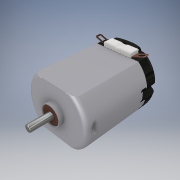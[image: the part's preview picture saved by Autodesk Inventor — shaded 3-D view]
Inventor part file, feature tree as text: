
AUTODESK INVENTOR PART (.ipt)
format: ipt  version: 2019 (Build 230136000, 136)  size: 1,063,424 bytes
history: native  units: mm
features: extrude x26, sketch x20, fillet x18, projected_geometry x6, plane x4, chamfer x3, mirror x2
ambient origin geometry x8: Origin, YZ Plane, XZ Plane, XY Plane, X Axis, Y Axis, Z Axis, Center Point
bodies: Solid1 (feature_tree)
feature tree (79):
  sketch  "Sketch1"  dims[d0=20.0mm d1=15.0mm d2=25.0mm d3=0.0mm d4=1.5mm]
  extrude  "Extrusion1"  Depth=15.0mm
  fillet  "Fillet1"  Radius=25.0mm
  fillet  "Fillet2"  Radius=1.5mm
  plane  "Work Plane1"
  extrude  "Extrusion2"  Depth=25.0mm TaperAngle=0.0deg
  extrude  "Extrusion3"  Depth=0.01mm TaperAngle=0.0deg
  extrude  "Extrusion4"  Depth=10.0mm
  sketch  "Sketch5"  dims[d12=10.0mm d13=4.0mm]
  extrude  "Extrusion5"  Depth=2.5mm
  extrude  "Extrusion6"  Depth=5.5mm
  extrude  "Extrusion7"  Depth=2.0mm
  extrude  "Extrusion8"  Depth=2.0mm TaperAngle=0.0deg
  sketch  "Sketch7"  dims[d17=1.0mm d18=5.5mm]
  extrude  "Extrusion10"  Depth=1.5mm TaperAngle=0.0deg
  extrude  "Extrusion11"  Depth=1.5mm
  extrude  "Extrusion12"  Depth=6.5mm TaperAngle=0.0deg
  extrude  "Extrusion9"  Depth=5.5mm
  extrude  "Extrusion13"  Depth=2.0mm
  chamfer  "Chamfer1"  Distance=1.5mm
  fillet  "Fillet4"  Radius=1.4mm
  fillet  "Fillet5"  Radius=0.01mm
  fillet  "Fillet6"  Radius=7.5mm
  fillet  "Fillet8"  Radius=7.0mm
  fillet  "Fillet9"  Radius=2.0mm
  fillet  "Fillet10"  Radius=4.0mm
  fillet  "Fillet11"  Radius=1.25mm
  fillet  "Fillet12"  Radius=8.0mm
  fillet  "Fillet13"  Radius=2.0mm
  extrude  "Extrusion14"  Depth=2.0mm TaperAngle=45.0deg
  sketch  "Sketch10"  dims[d26=0.05mm d27=0.0mm d28=1.5mm d29=0.0mm]
  extrude  "Extrusion15"  Depth=4.0mm
  extrude  "Extrusion16"  Depth=0.25mm
  plane  "Work Plane2"
  extrude  "Extrusion17"  Depth=0.25mm
  fillet  "Fillet14"  Radius=0.01mm
  plane  "Work Plane3"
  extrude  "Extrusion18"  Depth=0.25mm
  extrude  "Extrusion19"  Depth=4.25mm
  fillet  "Fillet16"  Radius=10.75mm
  mirror  "Mirror3"
  fillet  "Fillet15"  Radius=1.0mm
  fillet  "Fillet17"  Radius=1.5mm
  extrude  "Extrusion20"  Depth=0.1mm
  extrude  "Extrusion21"  Depth=0.25mm TaperAngle=0.0deg
  extrude  "Extrusion22"  Depth=0.25mm
  extrude  "Extrusion23"  Depth=0.25mm
  plane  "Work Plane4"
  extrude  "Extrusion24"  Depth=0.1mm TaperAngle=0.0deg
  chamfer  "Chamfer2"  Distance=10.0mm
  extrude  "Extrusion25"  Depth=0.1mm TaperAngle=0.0deg
  chamfer  "Chamfer3"  Distance=1.0mm
  fillet  "Fillet18"  [1 undecoded]
  extrude  "Extrusion26"  Depth=2.0mm
  mirror  "Mirror4"
  fillet  "Fillet19"  Radius=0.25mm
  fillet  "Fillet20"  Radius=1.75mm
  sketch  "Sketch3"  dims[d5=2.5mm d6=-5.0mm d7=25.0mm d8=0.0mm]
  sketch  "Sketch4"  dims[d9=0.25mm d10=0.01mm d11=0.0mm]
  sketch  "Sketch6"  dims[d14=2.5mm d15=0.0mm d16=2.5mm]
  sketch  "Sketch8"  dims[d19=4.0mm d20=2.0mm]
  projected_geometry  "Projected Loop1"
  sketch  "Sketch9"  dims[d21=0.01mm d23=2.0mm d24=0.0mm]
  sketch  "Sketch11"  dims[d30=1.0mm d31=0.0mm d32=1.5mm]
  sketch  "Sketch12"  dims[d33=1.25mm d34=6.5mm d35=0.0mm]
  projected_geometry  "Projected Loop2"
  sketch  "Sketch13"  dims[d36=6.0mm d37=5.5mm]
  sketch  "Sketch14"  dims[d38=0.01mm d39=2.0mm d40=1.5mm d41=0.0mm d42=1.4mm d43=0.0mm d44=0.01mm d45=7.5mm d46=0.0mm d47=7.0mm d48=2.0mm d49=4.0mm d50=1.25mm d51=8.0mm d52=2.0mm]
  projected_geometry  "Projected Loop3"
  sketch  "Sketch15"  dims[d53=0.75mm d54=0.0mm d55=0.75mm d56=2.0mm d57=45.0deg]
  sketch  "Sketch16"  dims[d58=1.0mm d59=4.0mm]
  sketch  "Sketch17"  dims[d60=0.25mm d62=0.25mm]
  projected_geometry  "Projected Loop4"
  sketch  "Sketch18"  dims[d63=0.5mm d64=0.25mm d65=0.01mm]
  sketch  "Sketch19"  dims[d66=0.1mm d67=0.25mm]
  sketch  "Sketch20"  dims[d68=4.0mm d69=4.25mm d70=10.75mm d71=1.0mm d72=0.0mm d74=1.5mm]
  sketch  "Sketch21"  dims[d75=5.0mm d76=5.0mm d77=0.25mm d78=0.0mm d79=0.25mm d80=0.25mm d81=0.05mm d82=0.0mm d83=10.0mm d87=1.0mm d88=0.0mm d90=1.0mm d91=-10.0mm d92=2.0mm d93=0.25mm d94=1.75mm d95=4.0mm d96=0.25mm d97=0.0mm d98=2.0mm d99=0.25mm d100=0.0mm d101=0.6mm d102=0.2mm d104=2.0mm d105=0.5mm d107=3.0mm d108=2.25mm d109=0.25mm d110=1.25mm d111=7.5mm d112=23.0mm d113=0.0mm d114=0.5mm d115=2.0mm d116=23.75mm d117=0.0mm d118=8.5mm d119=0.01mm d120=23.75mm d121=0.0mm d122=4.0mm d123=3.0mm d124=23.75mm d125=0.0mm d126=0.2mm d128=12.217305mm d129=3.75mm d130=2.0mm d131=0.0mm d132=0.35mm d133=2.0mm d134=45.0deg d135=1.25mm d136=0.375mm d137=0.375mm d139=1.0mm d140=2.0mm d141=0.0mm d142=0.15mm d143=2.0mm d144=45.0deg d145=0.25mm d146=0.01mm d147=0.01mm d148=0.01mm d149=2.0mm d150=0.0mm d151=0.01mm d152=0.05mm d153=0.001mm d154=0.1mm]
  projected_geometry  "Projected Loop5"
  projected_geometry  "Project Cut Edges1"
note: 1 required parameter value undecoded (feature->parameter linkage not recoverable at this tier; creation-order binding heuristic only, values carry confidence <= 0.55)
